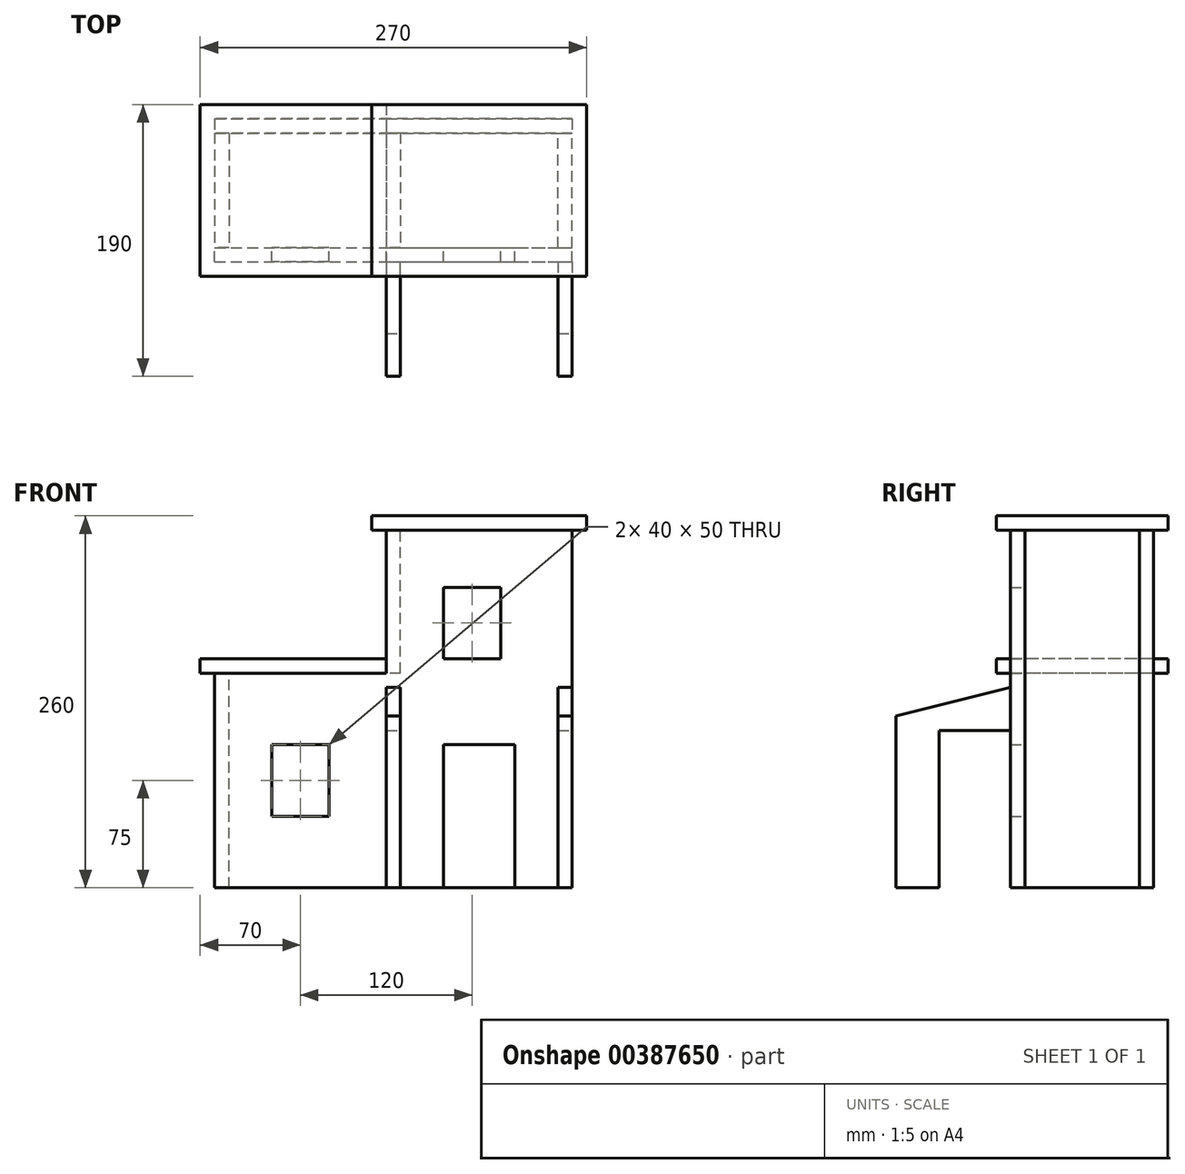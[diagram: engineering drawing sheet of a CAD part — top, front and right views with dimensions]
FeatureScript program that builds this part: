
annotation { "Feature Type Name" : "Feature", "Feature Type Description" : "" }
export const myFeature = defineFeature(function(context is Context, id is Id, definition is map)
    precondition{}
    {
        {
            var Q0;
            Q0=qCreatedBy(makeId("Front.planeOp"),FACE);
            var sketch = newSketch(context, id + "F0", { "sketchPlane" : qUnion([Q0])});
            skLineSegment(sketch, "E0.top", {"start": v(0, 100) * mm, "end": v(50, 100) * mm});
            skLineSegment(sketch, "E0.left", {"start": v(0, 0) * mm, "end": v(0, 100) * mm});
            skLineSegment(sketch, "E0.right", {"start": v(50, 0) * mm, "end": v(50, 100) * mm});
            skLineSegment(sketch, "E1.bottom", {"start": v(-160, 0) * mm, "end": v(0, 0) * mm});
            skLineSegment(sketch, "E1.top", {"start": v(-40, 250) * mm, "end": v(90, 250) * mm});
            skLineSegment(sketch, "E1.left", {"start": v(-160, 0) * mm, "end": v(-160, 150) * mm});
            skLineSegment(sketch, "E1.right", {"start": v(90, 0) * mm, "end": v(90, 250) * mm});
            skLineSegment(sketch, "E2.top", {"start": v(-160, 150) * mm, "end": v(-40, 150) * mm});
            skLineSegment(sketch, "E2.right", {"start": v(-40, 250) * mm, "end": v(-40, 150) * mm});
            skLineSegment(sketch, "E3.bottom", {"start": v(-80, 100) * mm, "end": v(-120, 100) * mm});
            skLineSegment(sketch, "E3.top", {"start": v(-80, 50) * mm, "end": v(-120, 50) * mm});
            skLineSegment(sketch, "E3.left", {"start": v(-80, 100) * mm, "end": v(-80, 50) * mm});
            skLineSegment(sketch, "E3.right", {"start": v(-120, 100) * mm, "end": v(-120, 50) * mm});
            skLineSegment(sketch, "E4.bottom", {"start": v(0, 210) * mm, "end": v(40, 210) * mm});
            skLineSegment(sketch, "E4.top", {"start": v(0, 160) * mm, "end": v(40, 160) * mm});
            skLineSegment(sketch, "E4.left", {"start": v(0, 210) * mm, "end": v(0, 160) * mm});
            skLineSegment(sketch, "E4.right", {"start": v(40, 210) * mm, "end": v(40, 160) * mm});
            skLineSegment(sketch, "E5.trimOffspring", {"start": v(50, 0) * mm, "end": v(90, 0) * mm});
            skSolve(sketch);
        }
        {
            var Q0;
            Q0 = qSketchRegion(id + "F0", true);
            extrude(context, id + "F1", {"entities" : qUnion([Q0]), "endBound" : BoundingType.SYMMETRIC, "depth" : 10 * mm});
        }
        {
            var Q0;
            Q0=makeQuery(id+"F1.opExtrude","CAP_FACE",FACE,{"disambiguationData":[OSD([sQuery(id+"F0.wireOp",EDGE,"E0.top"),sQuery(id+"F0.wireOp",EDGE,"E0.left"),sQuery(id+"F0.wireOp",EDGE,"E0.right"),sQuery(id+"F0.wireOp",EDGE,"E1.bottom"),sQuery(id+"F0.wireOp",EDGE,"E1.top"),sQuery(id+"F0.wireOp",EDGE,"E1.left"),sQuery(id+"F0.wireOp",EDGE,"E1.right"),sQuery(id+"F0.wireOp",EDGE,"E2.top"),sQuery(id+"F0.wireOp",EDGE,"E2.right"),sQuery(id+"F0.wireOp",EDGE,"E3.bottom"),sQuery(id+"F0.wireOp",EDGE,"E3.top"),sQuery(id+"F0.wireOp",EDGE,"E3.left"),sQuery(id+"F0.wireOp",EDGE,"E3.right"),sQuery(id+"F0.wireOp",EDGE,"E4.bottom"),sQuery(id+"F0.wireOp",EDGE,"E4.top"),sQuery(id+"F0.wireOp",EDGE,"E4.left"),sQuery(id+"F0.wireOp",EDGE,"E4.right"),sQuery(id+"F0.wireOp",EDGE,"E5.trimOffspring")])],"isStart":true});
            cPlane(context, id + "F2", {"entities" : qUnion([Q0]), "cplaneType" : CPlaneType.OFFSET, "offset" : 80 * mm, "width" : 150 * mm, "height" : 150 * mm});
        }
        {
            var Q0;
            Q0=qCreatedBy(id+"F2.planeOp",FACE);
            var sketch = newSketch(context, id + "F3", { "sketchPlane" : qUnion([Q0])});
            skLineSegment(sketch, "E6.0.0", {"start": v(-90, 0) * mm, "end": v(-50, 0) * mm});
            skLineSegment(sketch, "E6.0.4", {"start": v(0, 0) * mm, "end": v(160, 0) * mm});
            skLineSegment(sketch, "E6.0.5", {"start": v(160, 0) * mm, "end": v(160, 150) * mm});
            skLineSegment(sketch, "E6.0.6", {"start": v(160, 150) * mm, "end": v(40, 150) * mm});
            skLineSegment(sketch, "E6.0.7", {"start": v(40, 150) * mm, "end": v(40, 250) * mm});
            skLineSegment(sketch, "E6.0.8", {"start": v(40, 250) * mm, "end": v(-90, 250) * mm});
            skLineSegment(sketch, "E6.0.9", {"start": v(-90, 250) * mm, "end": v(-90, 0) * mm});
            skLineSegment(sketch, "E7", {"start": v(-50, 0) * mm, "end": v(0, 0) * mm});
            skSolve(sketch);
        }
        {
            var Q0;
            Q0=makeQuery(id+"F3.imprint","IMPRINT",FACE,{"disambiguationData":[TD([[makeQuery(id+"F3.imprint","IMPRINT",EDGE,{"derivedFrom":sQuery(id+"F3.wireOp",EDGE,"E6.0.0")}),1.0]])]});
            extrude(context, id + "F4", {"entities" : qUnion([Q0]), "depth" : 10 * mm});
        }
        {
            var Q0;
            Q0=makeQuery(id+"F1.opExtrude","SWEPT_FACE",FACE,{"disambiguationData":[OSD([sQuery(id+"F0.wireOp",EDGE,"E1.right")])]});
            var sketch = newSketch(context, id + "F5", { "sketchPlane" : qUnion([Q0])});
            skLineSegment(sketch, "E8.bottom", {"start": v(5, 250) * mm, "end": v(85, 250) * mm});
            skLineSegment(sketch, "E8.top", {"start": v(5, 0) * mm, "end": v(85, 0) * mm});
            skLineSegment(sketch, "E8.left", {"start": v(5, 250) * mm, "end": v(5, 0) * mm});
            skLineSegment(sketch, "E8.right", {"start": v(85, 250) * mm, "end": v(85, 0) * mm});
            skSolve(sketch);
        }
        {
            var Q0;
            Q0 = qSketchRegion(id + "F5", true);
            extrude(context, id + "F6", {"entities" : qUnion([Q0]), "oppositeDirection" : true, "depth" : 10 * mm});
        }
        {
            var Q0;
            Q0=makeQuery(id+"F4.opExtrude","SWEPT_FACE",FACE,{"disambiguationData":[OSD([sQuery(id+"F3.wireOp",EDGE,"E6.0.5")])]});
            var sketch = newSketch(context, id + "F7", { "sketchPlane" : qUnion([Q0])});
            skLineSegment(sketch, "E9.bottom", {"start": v(-85, 150) * mm, "end": v(-5, 150) * mm});
            skLineSegment(sketch, "E9.top", {"start": v(-85, 0) * mm, "end": v(-5, 0) * mm});
            skLineSegment(sketch, "E9.left", {"start": v(-85, 150) * mm, "end": v(-85, 0) * mm});
            skLineSegment(sketch, "E9.right", {"start": v(-5, 150) * mm, "end": v(-5, 0) * mm});
            skSolve(sketch);
        }
        {
            var Q0;
            Q0 = qSketchRegion(id + "F7", true);
            extrude(context, id + "F8", {"entities" : qUnion([Q0]), "oppositeDirection" : true, "depth" : 10 * mm});
        }
        {
            var Q0;
            Q0=makeQuery(id+"F4.opExtrude","SWEPT_FACE",FACE,{"disambiguationData":[OSD([sQuery(id+"F3.wireOp",EDGE,"E6.0.7")])]});
            var sketch = newSketch(context, id + "F9", { "sketchPlane" : qUnion([Q0])});
            skLineSegment(sketch, "E10.bottom", {"start": v(-85, 250) * mm, "end": v(-5, 250) * mm});
            skLineSegment(sketch, "E10.top", {"start": v(-85, 150) * mm, "end": v(-5, 150) * mm});
            skLineSegment(sketch, "E10.left", {"start": v(-85, 250) * mm, "end": v(-85, 150) * mm});
            skLineSegment(sketch, "E10.right", {"start": v(-5, 250) * mm, "end": v(-5, 150) * mm});
            skSolve(sketch);
        }
        {
            var Q0;
            Q0 = qSketchRegion(id + "F9", true);
            extrude(context, id + "F10", {"entities" : qUnion([Q0]), "oppositeDirection" : true, "depth" : 10 * mm});
        }
        {
            var Q0;
            Q0=makeQuery(id+"F1.opExtrude","SWEPT_FACE",FACE,{"disambiguationData":[OSD([sQuery(id+"F0.wireOp",EDGE,"E2.top")])]});
            var sketch = newSketch(context, id + "F11", { "sketchPlane" : qUnion([Q0])});
            skLineSegment(sketch, "E11.0", {"start": v(-170, 105) * mm, "end": v(-40, 105) * mm});
            skLineSegment(sketch, "E11.1", {"start": v(-170, -15) * mm, "end": v(-40, -15) * mm});
            skLineSegment(sketch, "E11.2", {"start": v(-170, -15) * mm, "end": v(-170, 5) * mm});
            skLineSegment(sketch, "E11.3", {"start": v(-170, 85) * mm, "end": v(-170, 5) * mm});
            skLineSegment(sketch, "E11.4", {"start": v(-170, 105) * mm, "end": v(-170, 85) * mm});
            skLineSegment(sketch, "E12", {"start": v(-40, 105) * mm, "end": v(-40, -15) * mm});
            skSolve(sketch);
        }
        {
            var Q0;
            Q0 = qSketchRegion(id + "F11", true);
            extrude(context, id + "F12", {"entities" : qUnion([Q0]), "depth" : 10 * mm});
        }
        {
            var Q0;
            Q0=makeQuery(id+"F1.opExtrude","SWEPT_FACE",FACE,{"disambiguationData":[OSD([sQuery(id+"F0.wireOp",EDGE,"E1.top")])]});
            var sketch = newSketch(context, id + "F13", { "sketchPlane" : qUnion([Q0])});
            skLineSegment(sketch, "E13.0", {"start": v(-50, 105) * mm, "end": v(-50, 85) * mm});
            skLineSegment(sketch, "E13.1", {"start": v(-50, 85) * mm, "end": v(-50, 5) * mm});
            skLineSegment(sketch, "E13.2", {"start": v(-50, 105) * mm, "end": v(100, 105) * mm});
            skLineSegment(sketch, "E13.3", {"start": v(-50, -15) * mm, "end": v(-50, 5) * mm});
            skLineSegment(sketch, "E13.4", {"start": v(100, 105) * mm, "end": v(100, 85) * mm});
            skLineSegment(sketch, "E13.5", {"start": v(100, 5) * mm, "end": v(100, 85) * mm});
            skLineSegment(sketch, "E13.6", {"start": v(100, -15) * mm, "end": v(100, 5) * mm});
            skLineSegment(sketch, "E13.7", {"start": v(-50, -15) * mm, "end": v(100, -15) * mm});
            skSolve(sketch);
        }
        {
            var Q0;
            Q0 = qSketchRegion(id + "F13", true);
            extrude(context, id + "F14", {"entities" : qUnion([Q0]), "depth" : 10 * mm});
        }
        {
            var Q0;
            Q0=makeQuery(id+"F1.opExtrude","CAP_FACE",FACE,{"disambiguationData":[OSD([sQuery(id+"F0.wireOp",EDGE,"E0.top"),sQuery(id+"F0.wireOp",EDGE,"E0.left"),sQuery(id+"F0.wireOp",EDGE,"E0.right"),sQuery(id+"F0.wireOp",EDGE,"E1.bottom"),sQuery(id+"F0.wireOp",EDGE,"E1.top"),sQuery(id+"F0.wireOp",EDGE,"E1.left"),sQuery(id+"F0.wireOp",EDGE,"E1.right"),sQuery(id+"F0.wireOp",EDGE,"E2.top"),sQuery(id+"F0.wireOp",EDGE,"E2.right"),sQuery(id+"F0.wireOp",EDGE,"E3.bottom"),sQuery(id+"F0.wireOp",EDGE,"E3.top"),sQuery(id+"F0.wireOp",EDGE,"E3.left"),sQuery(id+"F0.wireOp",EDGE,"E3.right"),sQuery(id+"F0.wireOp",EDGE,"E4.bottom"),sQuery(id+"F0.wireOp",EDGE,"E4.top"),sQuery(id+"F0.wireOp",EDGE,"E4.left"),sQuery(id+"F0.wireOp",EDGE,"E4.right"),sQuery(id+"F0.wireOp",EDGE,"E5.trimOffspring")])],"isStart":false});
            var sketch = newSketch(context, id + "F15", { "sketchPlane" : qUnion([Q0])});
            skLineSegment(sketch, "E14.bottom", {"start": v(-40, 0) * mm, "end": v(-30, 0) * mm});
            skLineSegment(sketch, "E14.top", {"start": v(-40, 140) * mm, "end": v(-30, 140) * mm});
            skLineSegment(sketch, "E14.left", {"start": v(-40, 0) * mm, "end": v(-40, 140) * mm});
            skLineSegment(sketch, "E14.right", {"start": v(-30, 0) * mm, "end": v(-30, 140) * mm});
            skLineSegment(sketch, "E15.bottom", {"start": v(80, 140) * mm, "end": v(90, 140) * mm});
            skLineSegment(sketch, "E15.top", {"start": v(80, 0) * mm, "end": v(90, 0) * mm});
            skLineSegment(sketch, "E15.left", {"start": v(80, 140) * mm, "end": v(80, 0) * mm});
            skLineSegment(sketch, "E15.right", {"start": v(90, 140) * mm, "end": v(90, 0) * mm});
            skSolve(sketch);
        }
        {
            var Q0;
            Q0 = qSketchRegion(id + "F15", true);
            extrude(context, id + "F16", {"entities" : qUnion([Q0]), "depth" : 80 * mm});
        }
        {
            var Q0;
            Q0=makeQuery(id+"F16.opExtrude","SWEPT_FACE",FACE,{"disambiguationData":[OSD([sQuery(id+"F15.wireOp",EDGE,"E15.right")])]});
            var sketch = newSketch(context, id + "F17", { "sketchPlane" : qUnion([Q0])});
            skLineSegment(sketch, "E16", {"start": v(-5, 140) * mm, "end": v(-85, 120) * mm});
            skLineSegment(sketch, "E17", {"start": v(-85, 120) * mm, "end": v(-85, 140) * mm});
            skLineSegment(sketch, "E18", {"start": v(-85, 140) * mm, "end": v(-5, 140) * mm});
            skLineSegment(sketch, "E19.bottom", {"start": v(-5, 0) * mm, "end": v(-55, 0) * mm});
            skLineSegment(sketch, "E19.top", {"start": v(-5, 110) * mm, "end": v(-55, 110) * mm});
            skLineSegment(sketch, "E19.left", {"start": v(-5, 0) * mm, "end": v(-5, 110) * mm});
            skLineSegment(sketch, "E19.right", {"start": v(-55, 0) * mm, "end": v(-55, 110) * mm});
            skSolve(sketch);
        }
        {
            var Q0;
            Q0 = qSketchRegion(id + "F17", true);
            var Q1;
            Q1=makeQuery(id+"F16.opExtrude","SWEPT_FACE",FACE,{"disambiguationData":[OSD([sQuery(id+"F15.wireOp",EDGE,"E14.left")])]});
            extrude(context, id + "F18", {"entities" : qUnion([Q0]), "operationType" : NewBodyOperationType.REMOVE, "endBound" : BoundingType.UP_TO_SURFACE, "oppositeDirection" : true, "endBoundEntityFace" : qUnion([Q1]), "depth" : 25 * mm});
        }
    });
